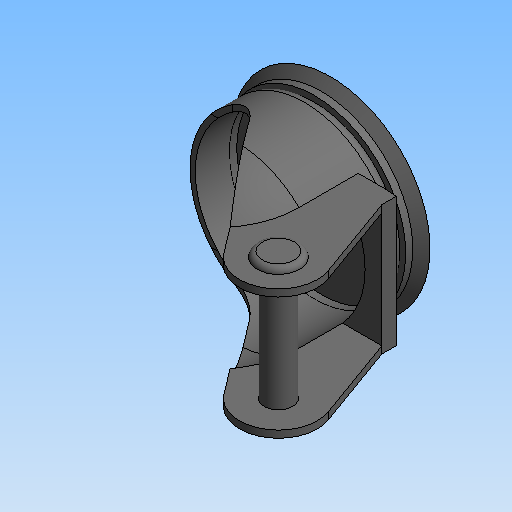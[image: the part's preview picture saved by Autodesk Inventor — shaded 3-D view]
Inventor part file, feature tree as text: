
AUTODESK INVENTOR PART (.ipt)
format: ipt  version: 2020 (Build 240168000, 168)  size: 248,320 bytes
history: native  units: mm (DEFAULTED — no unit token found)
features: sketch x10, extrude x7, revolve x3
ambient origin geometry x8: Origin, YZ Plane, XZ Plane, XY Plane, X Axis, Y Axis, Z Axis, Center Point
bodies: Solid1 (feature_tree), body_to_dummy_XY (feature_tree), body_to_dummy_YZ (feature_tree), body_to_dummy_ZX (feature_tree), body_to_dummy_X (feature_tree), body_to_dummy_Y (feature_tree), body_to_dummy_Z (feature_tree), body_to_dummy_Center (feature_tree), body_to_stopper_left_XY (feature_tree), body_to_stopper_left_YZ (feature_tree), body_to_stopper_left_ZX (feature_tree), body_to_stopper_left_X (feature_tree), body_to_stopper_left_Y (feature_tree), body_to_stopper_left_Z (feature_tree), body_to_stopper_left_Center (feature_tree), body_to_stopper_right_XY (feature_tree), body_to_stopper_right_YZ (feature_tree), body_to_stopper_right_ZX (feature_tree), body_to_stopper_right_X (feature_tree), body_to_stopper_right_Y (feature_tree), body_to_stopper_right_Z (feature_tree), body_to_stopper_right_Center (feature_tree), body_to_swivel_XY (feature_tree), body_to_swivel_YZ (feature_tree), body_to_swivel_ZX (feature_tree), body_to_swivel_X (feature_tree), body_to_swivel_Y (feature_tree), body_to_swivel_Z (feature_tree), body_to_swivel_Center (feature_tree), body_to_wheel_XY (feature_tree), body_to_wheel_YZ (feature_tree), body_to_wheel_ZX (feature_tree), body_to_wheel_X (feature_tree), body_to_wheel_Y (feature_tree), body_to_wheel_Z (feature_tree), body_to_wheel_Center (feature_tree)
feature tree (20):
  revolve  "Revolution1"  [1 undecoded]
  extrude  "Extrusion1"  Depth=100.0mm TaperAngle=0.0deg
  sketch  "Sketch_3"  dims[d7=24.076mm d8=0.0mm d9=360.0deg]
  extrude  "Extrusion2"  TaperAngle=360.0deg  [1 undecoded]
  extrude  "Extrusion3"  Depth=116.0mm TaperAngle=0.0deg
  extrude  "Extrusion4"  TaperAngle=360.0deg  [1 undecoded]
  revolve  "Revolution2"  [1 undecoded]
  extrude  "Extrusion5"  [1 undecoded]
  extrude  "Extrusion6"  [1 undecoded]
  extrude  "Extrusion7"  [1 undecoded]
  revolve  "Revolution3"  [1 undecoded]
  sketch  "Sketch_1"  dims[d0=360.0deg d1=56.0mm d2=0.0mm]
  sketch  "Sketch_2"  dims[d3=44.0mm d4=0.0mm d5=100.0mm d6=0.0mm]
  sketch  "Sketch_5"  dims[d14=36.6mm d15=0.0mm d16=360.0deg]
  sketch  "Sketch_4"  dims[d10=116.0mm d11=0.0mm d12=116.0mm d13=0.0mm]
  sketch  "Sketch_6"  dims[d17=0.0mm d18=0.0mm d19=0.0mm]
  sketch  "Sketch_7"
  sketch  "Sketch_8"
  sketch  "Sketch_9"
  sketch  "Sketch_10"
note: 8 required parameter values undecoded (feature->parameter linkage not recoverable at this tier; creation-order binding heuristic only, values carry confidence <= 0.55)